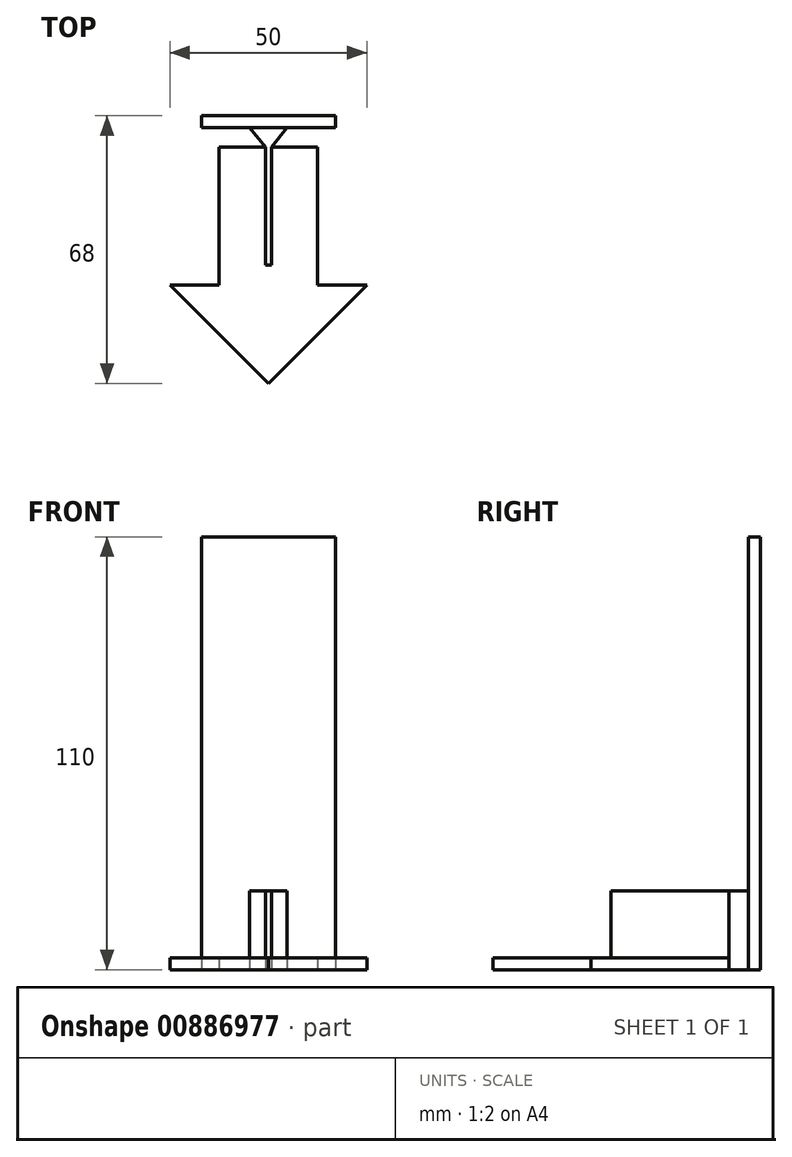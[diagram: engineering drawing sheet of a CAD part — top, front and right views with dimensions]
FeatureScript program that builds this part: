
annotation { "Feature Type Name" : "Feature", "Feature Type Description" : "" }
export const myFeature = defineFeature(function(context is Context, id is Id, definition is map)
    precondition{}
    {
        {
            var Q0;
            Q0=qCreatedBy(makeId("Top.planeOp"),FACE);
            var sketch = newSketch(context, id + "F0", { "sketchPlane" : qUnion([Q0])});
            skLineSegment(sketch, "E0.bottom", {"start": v(12.5, 30) * mm, "end": v(-12.5, 30) * mm});
            skLineSegment(sketch, "E0.top", {"start": v(12.5, -30) * mm, "end": v(-12.5, -30) * mm});
            skLineSegment(sketch, "E0.left", {"start": v(12.5, 30) * mm, "end": v(12.5, -30) * mm});
            skLineSegment(sketch, "E0.right", {"start": v(-12.5, 30) * mm, "end": v(-12.5, -30) * mm});
            skPoint(sketch, "E0.middle", {"position": v(0, 0) * mm});
            skLineSegment(sketch, "E1", {"start": v(0, -30) * mm, "end": v(-25, -5) * mm});
            skLineSegment(sketch, "E2", {"start": v(-25, -5) * mm, "end": v(25, -5) * mm});
            skLineSegment(sketch, "E3", {"start": v(25, -5) * mm, "end": v(0, -30) * mm});
            skLineSegment(sketch, "E4", {"start": v(0, -5) * mm, "end": v(0, -30) * mm});
            skLineSegment(sketch, "E5.bottom", {"start": v(-0.75, 0) * mm, "end": v(0.75, 0) * mm});
            skLineSegment(sketch, "E5.top", {"start": v(-0.75, 38) * mm, "end": v(0.75, 38) * mm});
            skLineSegment(sketch, "E5.left", {"start": v(-0.75, 0) * mm, "end": v(-0.75, 38) * mm});
            skLineSegment(sketch, "E5.right", {"start": v(0.75, 0) * mm, "end": v(0.75, 38) * mm});
            skLineSegment(sketch, "E6.bottom", {"start": v(17, 38) * mm, "end": v(-17, 38) * mm});
            skLineSegment(sketch, "E6.top", {"start": v(17, 35) * mm, "end": v(0.75, 35) * mm});
            skLineSegment(sketch, "E6.left", {"start": v(17, 38) * mm, "end": v(17, 35) * mm});
            skLineSegment(sketch, "E6.right", {"start": v(-17, 38) * mm, "end": v(-17, 35) * mm});
            skLineSegment(sketch, "E7.trimOffspring", {"start": v(-0.75, 35) * mm, "end": v(-17, 35) * mm});
            skLineSegment(sketch, "E8", {"start": v(-4.75, 35) * mm, "end": v(-0.75, 30) * mm});
            skLineSegment(sketch, "E9", {"start": v(0, 38) * mm, "end": v(0, 30) * mm, "construction": true});
            skLineSegment(sketch, "E10.MirrorCS", {"start": v(4.75, 35) * mm, "end": v(0.75, 30) * mm});
            skLineSegment(sketch, "E11", {"start": v(-0.75, 35) * mm, "end": v(0.75, 35) * mm});
            skSolve(sketch);
        }
        {
            var Q0;
            {var subQ13=sQuery(id+"F0.wireOp",EDGE,"E5.bottom");Q0=makeQuery(id+"F0.imprint","IMPRINT",FACE,{"disambiguationData":[TD([[makeQuery(id+"F0.imprint","IMPRINT",EDGE,{"derivedFrom":subQ13}),-1.0]])]});}
            var Q1;
            {var subQ5=sQuery(id+"F0.wireOp",EDGE,"E5.bottom");Q1=makeQuery(id+"F0.imprint","IMPRINT",FACE,{"disambiguationData":[TD([[makeQuery(id+"F0.imprint","IMPRINT",EDGE,{"derivedFrom":subQ5}),1.0]])]});}
            var Q2;
            {var subQ5=sQuery(id+"F0.wireOp",EDGE,"E4");Q2=makeQuery(id+"F0.imprint","IMPRINT",FACE,{"disambiguationData":[TD([[makeQuery(id+"F0.imprint","IMPRINT",EDGE,{"derivedFrom":subQ5}),-1.0]])]});}
            var Q3;
            {var subQ5=sQuery(id+"F0.wireOp",EDGE,"E4");Q3=makeQuery(id+"F0.imprint","IMPRINT",FACE,{"disambiguationData":[TD([[makeQuery(id+"F0.imprint","IMPRINT",EDGE,{"derivedFrom":subQ5}),1.0]])]});}
            var Q4;
            {var subQ0=sQuery(id+"F0.wireOp",EDGE,"E3");var subQ1=sQuery(id+"F0.wireOp",EDGE,"E0.left");var subQ2=makeQuery(id+"F0.imprint","INTERSECT",VERTEX,{"derivedFrom":[subQ1,subQ0]});Q4=makeQuery(id+"F0.imprint","IMPRINT",FACE,{"disambiguationData":[TD([[makeQuery(id+"F0.imprint","IMPRINT",EDGE,{"disambiguationData":[TD([[subQ2,1.0]])],"derivedFrom":subQ1}),1.0]])]});}
            var Q5;
            {var subQ0=sQuery(id+"F0.wireOp",EDGE,"E1");var subQ1=sQuery(id+"F0.wireOp",EDGE,"E0.right");var subQ2=makeQuery(id+"F0.imprint","INTERSECT",VERTEX,{"derivedFrom":[subQ1,subQ0]});Q5=makeQuery(id+"F0.imprint","IMPRINT",FACE,{"disambiguationData":[TD([[makeQuery(id+"F0.imprint","IMPRINT",EDGE,{"disambiguationData":[TD([[subQ2,1.0]])],"derivedFrom":subQ1}),-1.0]])]});}
            extrude(context, id + "F1", {"entities" : qUnion([Q0, Q1, Q2, Q3, Q4, Q5]), "depth" : 3 * mm, "offsetDistance" : 25 * mm});
        }
        {
            var Q0;
            {var subQ5=sQuery(id+"F0.wireOp",EDGE,"E11");Q0=makeQuery(id+"F0.imprint","IMPRINT",FACE,{"disambiguationData":[TD([[makeQuery(id+"F0.imprint","IMPRINT",EDGE,{"derivedFrom":subQ5}),-1.0]])]});}
            var Q1;
            {var subQ5=sQuery(id+"F0.wireOp",EDGE,"E5.bottom");Q1=makeQuery(id+"F0.imprint","IMPRINT",FACE,{"disambiguationData":[TD([[makeQuery(id+"F0.imprint","IMPRINT",EDGE,{"derivedFrom":subQ5}),1.0]])]});}
            var Q2;
            {var subQ3=sQuery(id+"F0.wireOp",EDGE,"E10.MirrorCS");Q2=makeQuery(id+"F0.imprint","IMPRINT",FACE,{"disambiguationData":[TD([[makeQuery(id+"F0.imprint","IMPRINT",EDGE,{"derivedFrom":subQ3}),-1.0]])]});}
            var Q3;
            {var subQ0=sQuery(id+"F0.wireOp",EDGE,"E8");Q3=makeQuery(id+"F0.imprint","IMPRINT",FACE,{"disambiguationData":[TD([[makeQuery(id+"F0.imprint","IMPRINT",EDGE,{"derivedFrom":subQ0}),1.0]])]});}
            extrude(context, id + "F2", {"entities" : qUnion([Q0, Q1, Q2, Q3]), "operationType" : NewBodyOperationType.ADD, "depth" : 20 * mm, "offsetDistance" : 25 * mm});
        }
        {
            var Q0;
            {var subQ0=sQuery(id+"F0.wireOp",EDGE,"E6.right");Q0=makeQuery(id+"F0.imprint","IMPRINT",FACE,{"disambiguationData":[TD([[makeQuery(id+"F0.imprint","IMPRINT",EDGE,{"derivedFrom":subQ0}),1.0]])]});}
            var Q1;
            {var subQ0=sQuery(id+"F0.wireOp",EDGE,"E5.top");Q1=makeQuery(id+"F0.imprint","IMPRINT",FACE,{"disambiguationData":[TD([[makeQuery(id+"F0.imprint","IMPRINT",EDGE,{"derivedFrom":subQ0}),-1.0]])]});}
            var Q2;
            {var subQ4=sQuery(id+"F0.wireOp",EDGE,"E6.left");Q2=makeQuery(id+"F0.imprint","IMPRINT",FACE,{"disambiguationData":[TD([[makeQuery(id+"F0.imprint","IMPRINT",EDGE,{"derivedFrom":subQ4}),-1.0]])]});}
            extrude(context, id + "F3", {"entities" : qUnion([Q0, Q1, Q2]), "operationType" : NewBodyOperationType.ADD, "depth" : 110 * mm, "offsetDistance" : 25 * mm});
        }
    });
